# Revit family: IEK_Держатель_Полоса-пруток_25-40мм-6-10мм_Опорный_Оцинкованная сталь
name_source: partatom
category: Обобщенные модели
units: mm (PartAtom-declared; Revit-internal decimal feet)

## family parameters
Может служить основой для арматурных стержней = Нет
Общий = Да
Основа = Грань
При загрузке вырезать с полостями = Нет
Размер круглого соединителя = Использовать диаметр
Тип детали = Нормальный
Точка расчета площади = Нет

## types (1)
- IEK_Держатель_Полоса-пруток_25-40мм-6-10мм_Опорный_Оцинкованная сталь
    ADSK_URL страницы изделия = https://www.iek.ru
    ADSK_Версия Revit = 2019
    ADSK_Версия семейства = 1.0
    ADSK_Группирование = VIII. ЭЛЕМЕНТЫ ВНЕШНЕЙ МОЛНИЕЗАЩИТЫ
    ADSK_Единица измерения = шт
    ADSK_Завод-изготовитель = IEK
    ADSK_Код изделия = ZDP51-11-1-16-40
    ADSK_Масса = 0.25
    ADSK_Материал = Сталь оцинкованная
    ADSK_Наименование = Дер. опорный пол./пруток 25-40мм/6-10мм оц. сталь IEK
    IEK_URL = https://www.iek.ru
    IEK_Описание = Универсальная конструкция держателя позволяет использовать его с проводниками различной формы и габаритами.
    IEK_Цена за единицу = 580
    KSI_CMa_Строительные материалы = 24.10.35.000.08.3.05.06-0001
    Отметка по умолчанию = 0 мм

## geometry (parser evidence)
native form markers: Blend x1
no freeform markers — native parametric forms only
